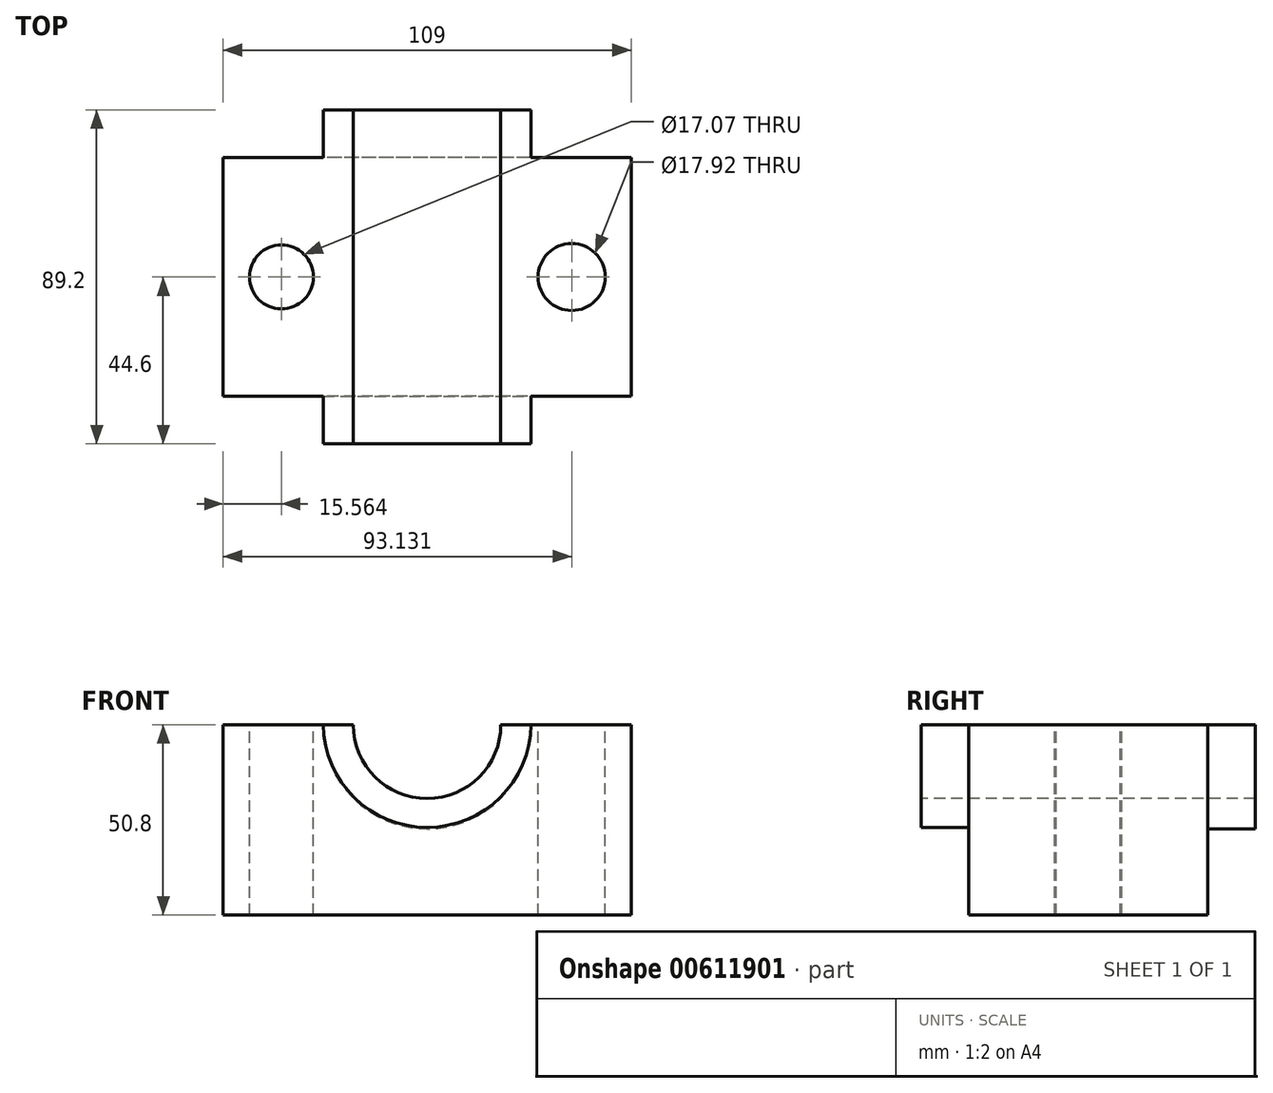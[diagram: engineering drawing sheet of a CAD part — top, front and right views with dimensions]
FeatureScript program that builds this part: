
annotation { "Feature Type Name" : "Feature", "Feature Type Description" : "" }
export const myFeature = defineFeature(function(context is Context, id is Id, definition is map)
    precondition{}
    {
        {
            var Q0;
            Q0=qCreatedBy(makeId("Top.planeOp"),FACE);
            var sketch = newSketch(context, id + "F0", { "sketchPlane" : qUnion([Q0])});
            skLineSegment(sketch, "E0.bottom", {"start": v(54.5, 31.9) * mm, "end": v(-54.5, 31.9) * mm});
            skLineSegment(sketch, "E0.top", {"start": v(54.5, -31.9) * mm, "end": v(-54.5, -31.9) * mm});
            skLineSegment(sketch, "E0.left", {"start": v(54.5, 31.9) * mm, "end": v(54.5, -31.9) * mm});
            skLineSegment(sketch, "E0.right", {"start": v(-54.5, 31.9) * mm, "end": v(-54.5, -31.9) * mm});
            skPoint(sketch, "E0.middle", {"position": v(0, 0) * mm});
            skSolve(sketch);
        }
        {
            var Q0;
            Q0=makeQuery(id+"F0.imprint","IMPRINT",FACE,{"disambiguationData":[TD([[makeQuery(id+"F0.imprint","IMPRINT",EDGE,{"derivedFrom":sQuery(id+"F0.wireOp",EDGE,"E0.bottom")}),1.0]])]});
            extrude(context, id + "F1", {"entities" : qUnion([Q0]), "depth" : 50.8 * mm, "offsetDistance" : 25.4 * mm});
        }
        {
            var Q0;
            Q0=makeQuery(id+"F1.opExtrude","SWEPT_FACE",FACE,{"disambiguationData":[OSD([sQuery(id+"F0.wireOp",EDGE,"E0.top")])]});
            var sketch = newSketch(context, id + "F2", { "sketchPlane" : qUnion([Q0])});
            skArc(sketch, "E1", {"start": v(-19.7, 50.8) * mm, "mid": v(0, 31.1) * mm, "end": v(19.7, 50.8) * mm});
            skSolve(sketch);
        }
        {
            var Q0;
            {var subQ3=sQuery(id+"F2.wireOp",EDGE,"E1");Q0=makeQuery(id+"F2.imprint","IMPRINT",FACE,{"disambiguationData":[TD([[makeQuery(id+"F2.imprint","IMPRINT",EDGE,{"derivedFrom":subQ3}),-1.0]])]});}
            var sketch = newSketch(context, id + "F3", { "sketchPlane" : qUnion([Q0])});
            skArc(sketch, "E2", {"start": v(-27.76, 51.46) * mm, "mid": v(0, 23.39) * mm, "end": v(27.76, 51.46) * mm});
            skSolve(sketch);
        }
        {
            var Q0;
            {var subQ0=sQuery(id+"F2.wireOp",EDGE,"E1");Q0=makeQuery(id+"F2.imprint","IMPRINT",FACE,{"disambiguationData":[TD([[makeQuery(id+"F2.imprint","IMPRINT",EDGE,{"derivedFrom":subQ0}),1.0]])]});}
            extrude(context, id + "F4", {"entities" : qUnion([Q0]), "operationType" : NewBodyOperationType.REMOVE, "oppositeDirection" : true, "depth" : 89.92 * mm, "offsetDistance" : 25.4 * mm});
        }
        {
            var Q0;
            {var subQ3=sQuery(id+"F2.wireOp",EDGE,"E1");var subQ8=makeQuery(id+"F2.imprint","IMPRINT",EDGE,{"derivedFrom":subQ3});Q0=makeQuery(id+"F3.imprint","IMPRINT",FACE,{"disambiguationData":[TD([[makeQuery(id+"F3.imprint","IMPRINT",EDGE,{"derivedFrom":subQ8}),-1.0]])]});}
            extrude(context, id + "F5", {"entities" : qUnion([Q0]), "operationType" : NewBodyOperationType.ADD, "depth" : 12.7 * mm, "offsetDistance" : 25.4 * mm});
        }
        {
            var Q0;
            Q0=makeQuery(id+"F1.opExtrude","SWEPT_FACE",FACE,{"disambiguationData":[OSD([sQuery(id+"F0.wireOp",EDGE,"E0.bottom")])]});
            var sketch = newSketch(context, id + "F6", { "sketchPlane" : qUnion([Q0])});
            skCircle(sketch, "E3", {"center": v(0, 50.8) * mm, "radius": 27.8 * mm});
            skSolve(sketch);
        }
        {
            var Q0;
            {var subQ1=sQuery(id+"F0.wireOp",EDGE,"E0.bottom");var subQ2=makeQuery(id+"F1.opExtrude","SWEPT_FACE",FACE,{"disambiguationData":[OSD([subQ1])]});var subQ3=makeQuery(id+"F4.opExtrude","SWEPT_FACE",FACE,{"disambiguationData":[OSD([sQuery(id+"F2.wireOp",EDGE,"E1")])]});var subQ12=makeQuery(id+"F4.boolean.opBoolean","INTERSECT",EDGE,{"derivedFrom":[subQ2,subQ3]});Q0=makeQuery(id+"F6.imprint","IMPRINT",FACE,{"disambiguationData":[TD([[makeQuery(id+"F6.imprint","IMPRINT",EDGE,{"derivedFrom":subQ12}),1.0]])]});}
            extrude(context, id + "F7", {"entities" : qUnion([Q0]), "operationType" : NewBodyOperationType.ADD, "depth" : 12.7 * mm, "offsetDistance" : 25.4 * mm});
        }
        {
            var Q0;
            {var subQ0=sQuery(id+"F0.wireOp",EDGE,"E0.bottom");var subQ2=sQuery(id+"F2.wireOp",EDGE,"E1");var subQ4=sQuery(id+"F0.wireOp",EDGE,"E0.left");var subQ5=sQuery(id+"F0.wireOp",EDGE,"E0.top");var subQ6=makeQuery(id+"F1.opExtrude","CAP_FACE",FACE,{"disambiguationData":[OSD([subQ0,subQ5,subQ4,sQuery(id+"F0.wireOp",EDGE,"E0.right")])],"isStart":false});var subQ7=makeQuery(id+"F1.opExtrude","SWEPT_FACE",FACE,{"disambiguationData":[OSD([subQ4])]});var subQ8=makeQuery(id+"F4.boolean.opBoolean","SPLIT",EDGE,{"disambiguationData":[TD([subQ7])],"derivedFrom":makeQuery(id+"F1.opExtrude","CAP_EDGE",EDGE,{"disambiguationData":[OSD([subQ0])],"isStart":false})});var subQ9=makeQuery(id+"F1.opExtrude","CAP_EDGE",EDGE,{"disambiguationData":[OSD([subQ5])],"isStart":false});var subQ10=makeQuery(id+"F2.imprint","IMPRINT",EDGE,{"disambiguationData":[TD([[makeQuery(id+"F2.imprint","INTERSECT",VERTEX,{"disambiguationData":[OD(1.0)],"derivedFrom":[subQ9,subQ2]}),1.0]])],"derivedFrom":subQ9});Q0=makeQuery(id+"F7.boolean.opBoolean","MERGE",FACE,{"derivedFrom":[makeQuery(id+"F5.boolean.opBoolean","MERGE",FACE,{"derivedFrom":[makeQuery(id+"F4.boolean.opBoolean","SPLIT",FACE,{"disambiguationData":[TD([subQ7])],"derivedFrom":subQ6}),makeQuery(id+"F5.opExtrude","SWEPT_FACE",FACE,{"disambiguationData":[OSD([subQ5]),TDD([makeQuery(id+"F3.imprint","IMPRINT",EDGE,{"disambiguationData":[TD([[makeQuery(id+"F3.imprint","INTERSECT",VERTEX,{"derivedFrom":[makeQuery(id+"F2.imprint","IMPRINT",EDGE,{"derivedFrom":subQ2}),subQ10]}),1.0]])],"derivedFrom":subQ10})])]})]}),makeQuery(id+"F7.opExtrude","SWEPT_FACE",FACE,{"disambiguationData":[OSD([subQ0]),TDD([makeQuery(id+"F6.imprint","IMPRINT",EDGE,{"disambiguationData":[TD([[makeQuery(id+"F6.imprint","INTERSECT",VERTEX,{"derivedFrom":[subQ8,sQuery(id+"F6.wireOp",EDGE,"E3")]}),-1.0]])],"derivedFrom":subQ8})])]})]});}
            var sketch = newSketch(context, id + "F8", { "sketchPlane" : qUnion([Q0])});
            skCircle(sketch, "E4", {"center": v(37.71, 0) * mm, "radius": 8.56 * mm});
            skCircle(sketch, "E5", {"center": v(-38.94, 0) * mm, "radius": 8.54 * mm});
            skSolve(sketch);
        }
        {
            var Q0;
            Q0=makeQuery(id+"F8.imprint","IMPRINT",FACE,{"disambiguationData":[TD([[makeQuery(id+"F8.imprint","IMPRINT",EDGE,{"derivedFrom":sQuery(id+"F8.wireOp",EDGE,"E5")}),1.0]])]});
            extrude(context, id + "F9", {"entities" : qUnion([Q0]), "operationType" : NewBodyOperationType.REMOVE, "oppositeDirection" : true, "depth" : 76.7 * mm, "offsetDistance" : 25.4 * mm});
        }
        {
            var Q0;
            {var subQ0=sQuery(id+"F0.wireOp",EDGE,"E0.bottom");var subQ2=sQuery(id+"F2.wireOp",EDGE,"E1");var subQ4=sQuery(id+"F0.wireOp",EDGE,"E0.left");var subQ5=sQuery(id+"F0.wireOp",EDGE,"E0.top");var subQ6=makeQuery(id+"F1.opExtrude","CAP_FACE",FACE,{"disambiguationData":[OSD([subQ0,subQ5,subQ4,sQuery(id+"F0.wireOp",EDGE,"E0.right")])],"isStart":false});var subQ7=makeQuery(id+"F1.opExtrude","SWEPT_FACE",FACE,{"disambiguationData":[OSD([subQ4])]});var subQ8=makeQuery(id+"F4.boolean.opBoolean","SPLIT",EDGE,{"disambiguationData":[TD([subQ7])],"derivedFrom":makeQuery(id+"F1.opExtrude","CAP_EDGE",EDGE,{"disambiguationData":[OSD([subQ0])],"isStart":false})});var subQ9=makeQuery(id+"F1.opExtrude","CAP_EDGE",EDGE,{"disambiguationData":[OSD([subQ5])],"isStart":false});var subQ10=makeQuery(id+"F2.imprint","IMPRINT",EDGE,{"disambiguationData":[TD([[makeQuery(id+"F2.imprint","INTERSECT",VERTEX,{"disambiguationData":[OD(1.0)],"derivedFrom":[subQ9,subQ2]}),1.0]])],"derivedFrom":subQ9});Q0=makeQuery(id+"F7.boolean.opBoolean","MERGE",FACE,{"derivedFrom":[makeQuery(id+"F5.boolean.opBoolean","MERGE",FACE,{"derivedFrom":[makeQuery(id+"F4.boolean.opBoolean","SPLIT",FACE,{"disambiguationData":[TD([subQ7])],"derivedFrom":subQ6}),makeQuery(id+"F5.opExtrude","SWEPT_FACE",FACE,{"disambiguationData":[OSD([subQ5]),TDD([makeQuery(id+"F3.imprint","IMPRINT",EDGE,{"disambiguationData":[TD([[makeQuery(id+"F3.imprint","INTERSECT",VERTEX,{"derivedFrom":[makeQuery(id+"F2.imprint","IMPRINT",EDGE,{"derivedFrom":subQ2}),subQ10]}),1.0]])],"derivedFrom":subQ10})])]})]}),makeQuery(id+"F7.opExtrude","SWEPT_FACE",FACE,{"disambiguationData":[OSD([subQ0]),TDD([makeQuery(id+"F6.imprint","IMPRINT",EDGE,{"disambiguationData":[TD([[makeQuery(id+"F6.imprint","INTERSECT",VERTEX,{"derivedFrom":[subQ8,sQuery(id+"F6.wireOp",EDGE,"E3")]}),-1.0]])],"derivedFrom":subQ8})])]})]});}
            var sketch = newSketch(context, id + "F10", { "sketchPlane" : qUnion([Q0])});
            skCircle(sketch, "E6", {"center": v(38.63, 0) * mm, "radius": 8.96 * mm});
            skSolve(sketch);
        }
        {
            var Q0;
            Q0=makeQuery(id+"F10.imprint","IMPRINT",FACE,{"disambiguationData":[TD([[makeQuery(id+"F10.imprint","IMPRINT",EDGE,{"derivedFrom":sQuery(id+"F10.wireOp",EDGE,"E6")}),1.0]])]});
            extrude(context, id + "F11", {"entities" : qUnion([Q0]), "operationType" : NewBodyOperationType.REMOVE, "oppositeDirection" : true, "depth" : 88.4 * mm, "offsetDistance" : 25.4 * mm});
        }
    });
